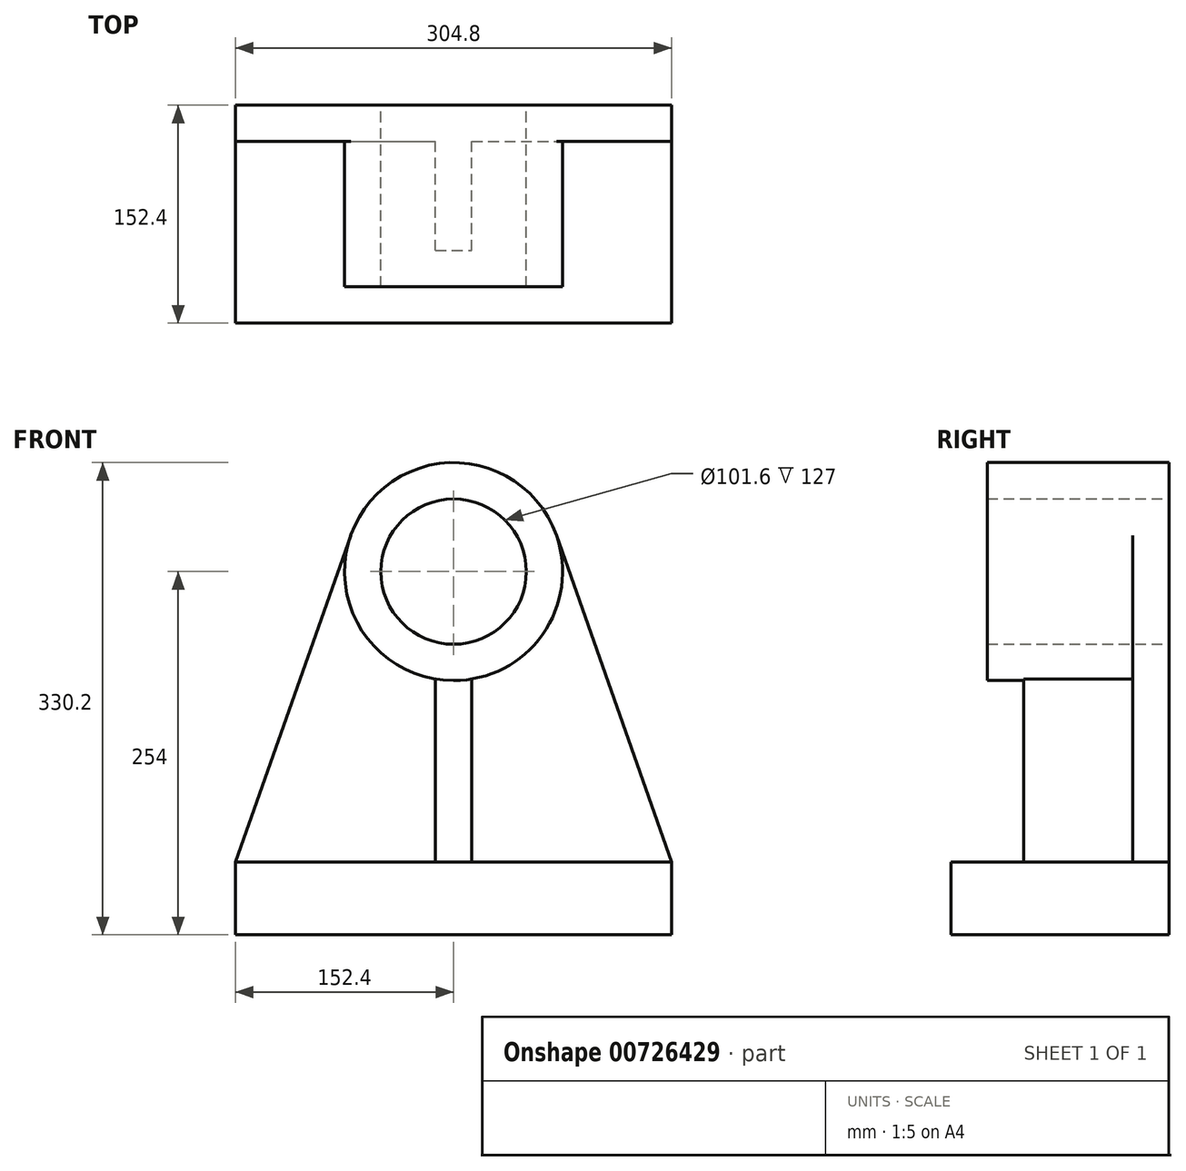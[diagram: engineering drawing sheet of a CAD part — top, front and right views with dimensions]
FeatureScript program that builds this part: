
annotation { "Feature Type Name" : "Feature", "Feature Type Description" : "" }
export const myFeature = defineFeature(function(context is Context, id is Id, definition is map)
    precondition{}
    {
        {
            var Q0;
            Q0=qCreatedBy(makeId("Front.planeOp"),FACE);
            var sketch = newSketch(context, id + "F0", { "sketchPlane" : qUnion([Q0])});
            skCircle(sketch, "E0", {"center": v(0, 0) * mm, "radius": 50.8 * mm});
            skCircle(sketch, "E1", {"center": v(0, 0) * mm, "radius": 76.2 * mm});
            skCircle(sketch, "E2", {"center": v(0, 0) * mm, "radius": 12.7 * mm});
            skLineSegment(sketch, "E3", {"start": v(-12.7, 0) * mm, "end": v(-12.7, -203.2) * mm});
            skLineSegment(sketch, "E4", {"start": v(12.7, 0) * mm, "end": v(12.7, -203.2) * mm});
            skLineSegment(sketch, "E5", {"start": v(-12.7, -203.2) * mm, "end": v(152.4, -203.2) * mm});
            skLineSegment(sketch, "E6", {"start": v(152.4, -203.2) * mm, "end": v(152.4, -254) * mm});
            skLineSegment(sketch, "E7", {"start": v(152.4, -254) * mm, "end": v(-152.4, -254) * mm});
            skLineSegment(sketch, "E8", {"start": v(-152.4, -254) * mm, "end": v(-152.4, -203.2) * mm});
            skLineSegment(sketch, "E9", {"start": v(-152.4, -203.2) * mm, "end": v(-12.7, -203.2) * mm});
            skLineSegment(sketch, "E10", {"start": v(-152.4, -203.2) * mm, "end": v(-71.87, 25.33) * mm});
            skLineSegment(sketch, "E11", {"start": v(152.4, -203.2) * mm, "end": v(71.87, 25.33) * mm});
            skSolve(sketch);
        }
        {
            var Q0;
            {var subQ0=sQuery(id+"F0.wireOp",EDGE,"E3");var subQ1=sQuery(id+"F0.wireOp",EDGE,"E0");var subQ2=makeQuery(id+"F0.imprint","INTERSECT",VERTEX,{"derivedFrom":[subQ1,subQ0]});Q0=makeQuery(id+"F0.imprint","IMPRINT",FACE,{"disambiguationData":[TD([[makeQuery(id+"F0.imprint","IMPRINT",EDGE,{"disambiguationData":[TD([[subQ2,-1.0]])],"derivedFrom":subQ1}),-1.0]])]});}
            var Q1;
            {var subQ5=sQuery(id+"F0.wireOp",EDGE,"E3");var subQ7=sQuery(id+"F0.wireOp",EDGE,"E0");var subQ8=makeQuery(id+"F0.imprint","INTERSECT",VERTEX,{"derivedFrom":[subQ7,subQ5]});Q1=makeQuery(id+"F0.imprint","IMPRINT",FACE,{"disambiguationData":[TD([[makeQuery(id+"F0.imprint","IMPRINT",EDGE,{"disambiguationData":[TD([[subQ8,1.0]])],"derivedFrom":subQ7}),-1.0]])]});}
            extrude(context, id + "F1", {"entities" : qUnion([Q0, Q1]), "depth" : 127 * mm, "offsetDistance" : 25.4 * mm});
        }
        {
            var Q0;
            {var subQ4=sQuery(id+"F0.wireOp",EDGE,"E9");Q0=makeQuery(id+"F0.imprint","IMPRINT",FACE,{"disambiguationData":[TD([[makeQuery(id+"F0.imprint","IMPRINT",EDGE,{"derivedFrom":subQ4}),1.0]])]});}
            var Q1;
            {var subQ0=sQuery(id+"F0.wireOp",EDGE,"E11");Q1=makeQuery(id+"F0.imprint","IMPRINT",FACE,{"disambiguationData":[TD([[makeQuery(id+"F0.imprint","IMPRINT",EDGE,{"derivedFrom":subQ0}),1.0]])]});}
            extrude(context, id + "F2", {"entities" : qUnion([Q0, Q1]), "operationType" : NewBodyOperationType.ADD, "depth" : 25.4 * mm, "offsetDistance" : 25.4 * mm});
        }
        {
            var Q0;
            {var subQ0=sQuery(id+"F0.wireOp",EDGE,"E6");Q0=makeQuery(id+"F0.imprint","IMPRINT",FACE,{"disambiguationData":[TD([[makeQuery(id+"F0.imprint","IMPRINT",EDGE,{"derivedFrom":subQ0}),-1.0]])]});}
            extrude(context, id + "F3", {"entities" : qUnion([Q0]), "operationType" : NewBodyOperationType.ADD, "depth" : 152.4 * mm, "offsetDistance" : 25.4 * mm});
        }
        {
            var Q0;
            {var subQ0=sQuery(id+"F0.wireOp",EDGE,"E3");var subQ1=sQuery(id+"F0.wireOp",EDGE,"E1");var subQ2=makeQuery(id+"F0.imprint","INTERSECT",VERTEX,{"derivedFrom":[subQ1,subQ0]});Q0=makeQuery(id+"F0.imprint","IMPRINT",FACE,{"disambiguationData":[TD([[makeQuery(id+"F0.imprint","IMPRINT",EDGE,{"disambiguationData":[TD([[subQ2,-1.0]])],"derivedFrom":subQ1}),-1.0]])]});}
            extrude(context, id + "F4", {"entities" : qUnion([Q0]), "operationType" : NewBodyOperationType.ADD, "depth" : 101.6 * mm, "offsetDistance" : 25.4 * mm});
        }
    });
